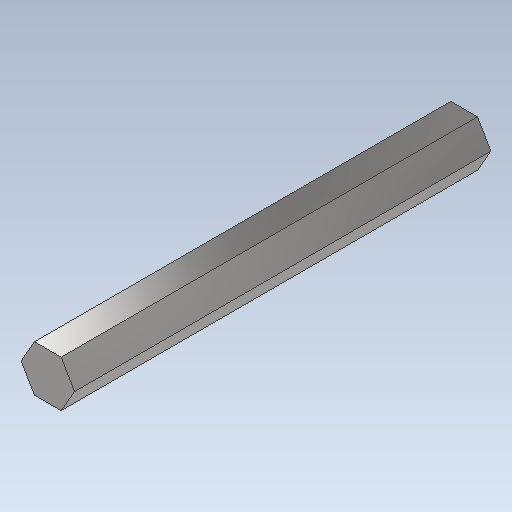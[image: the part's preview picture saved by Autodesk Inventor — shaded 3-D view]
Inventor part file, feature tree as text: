
AUTODESK INVENTOR PART (.ipt)
format: ipt  version: 2023 (Build 270158000, 158)  size: 94,720 bytes
history: native  units: in
note: dims shown in document units (in); Inventor stores cm internally (conversion verified against a paired STEP export)
features: other x3, sketch x1
ambient origin geometry x8: Origin, YZ Plane, XZ Plane, XY Plane, X Axis, Y Axis, Z Axis, Center Point
bodies: Solid1 (feature_tree)
feature tree (4):
  other  "Ch-1-01-0.5x4.5HexShaft.ipt"
  other  "Solid1::Ch-1-01-0.5x4.5HexShaft.ipt"
  other  "TaggingFeature1"
  sketch  "Sketch1"  dims[d0=0.3937in]
